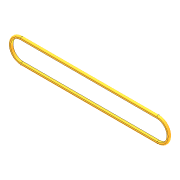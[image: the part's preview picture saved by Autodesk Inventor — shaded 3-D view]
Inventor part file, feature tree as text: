
AUTODESK INVENTOR PART (.ipt)
format: ipt  version: 2012 (Build 160160000, 160)  size: 93,184 bytes
history: native  units: in
note: dims shown in document units (in); Inventor stores cm internally (conversion verified against a paired STEP export)
features: extrude x1, fillet x1, sketch x1
ambient origin geometry x8: Origin, YZ Plane, XZ Plane, XY Plane, X Axis, Y Axis, Z Axis, Center Point
bodies: Solid1 (feature_tree)
feature tree (3):
  extrude  "Extrusion1"  Depth=10.25in
  fillet  "Fillet1"  Radius=0.1875in
  sketch  "Sketch1"  dims[d0=0.75in d1=10.25in d2=0.1875in d3=0.1875in d4=0.0in d5=0.0938in]
